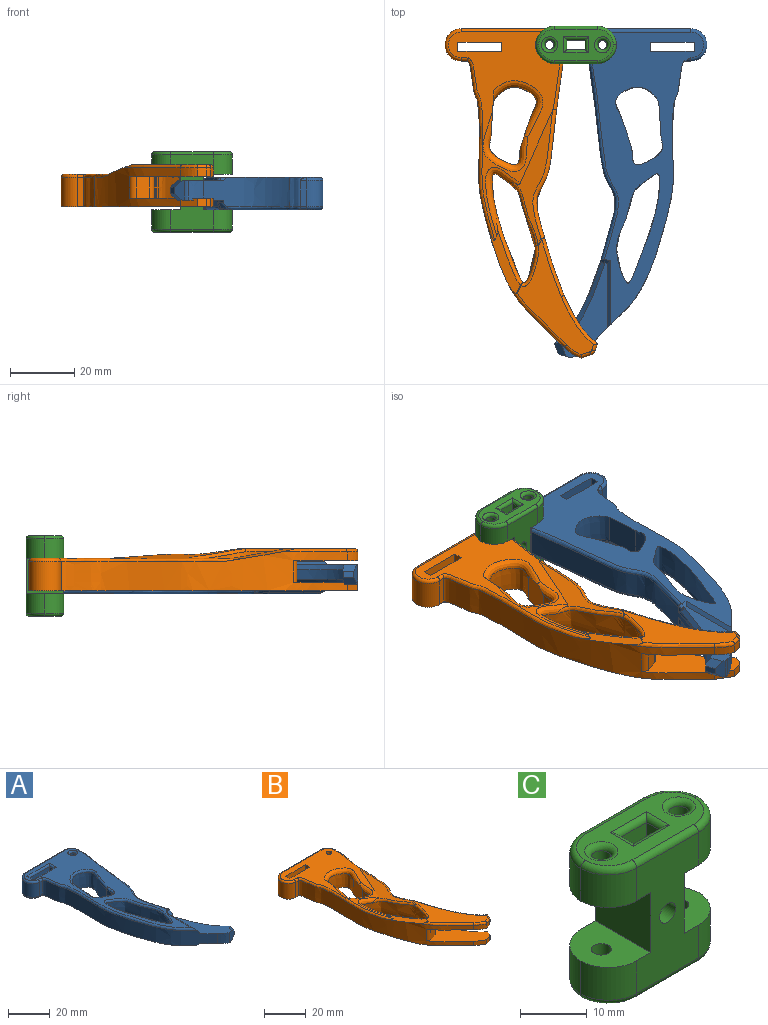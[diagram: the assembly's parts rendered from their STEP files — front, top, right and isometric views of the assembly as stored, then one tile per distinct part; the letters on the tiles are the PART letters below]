
ASSEMBLY  parts=3 mates=1
PART A: 74 faces, bbox 48.7x103.1x14 mm
  f0: plane 6x3.17mm, normal (0.32,-0.95,0), area 14.9mm2, adj f1,f25,f27,f28,f29,f30
  f1: plane 3.17x2mm, normal (0.94,-0.35,0), area 6.8mm2, adj f0,f2,f29,f30
  f2: extruded ~18.6x12mm, area 56.7mm2, adj f1,f8,f29,f30,f31,f33,f36,f45
  f3: extruded ~6x4.74mm, area 34.4mm2, adj f4,f25,f27,f28
  f4: extruded ~89.8x31.96mm, area 853mm2, adj f3,f7,f9,f14,f27,f28,f35,f44
  f5: plane 0.21x0.2mm, normal (0,-1,0), area 0mm2, adj f32,f37,f58
  f6: plane 88.13x34.8mm, normal (0,0,1), area 889.6mm2, adj f48,f49,f50,f51,f52,f53,f54,f60
  f7: plane 16.61x1mm, normal (1,0,0), area 16.6mm2, adj f4,f28,f35,f55
  f8: extruded ~72.26x8.46mm, area 526.1mm2, adj f2,f17,f36,f37,f38,f45,f46,f47
  f9: plane 91.35x34.8mm, normal (0,0,-1), area 1198.8mm2, adj f4,f10,f11,f15,f16,f20,f21,f22
  f10: plane 9x2.8mm, normal (1,0,0), area 25.2mm2, adj f9,f11,f15,f64
  f11: plane 13.5x9mm, normal (0,-1,0), area 121.5mm2, adj f9,f10,f26,f65
  f12: plane 8x4.46mm, normal (1,0,0), area 35.7mm2, adj f17,f19,f40,f50
  f13: plane 26.8x8mm, normal (0,1,0), area 214.4mm2, adj f18,f19,f42,f52
  f14: plane 8x1.91mm, normal (0,-1,0), area 15.3mm2, adj f4,f18,f44,f54
  f15: plane 13.5x9mm, normal (0,1,0), area 121.5mm2, adj f9,f10,f26,f66
  f16: cylinder r=1.35mm len=9mm, axis (0,0,-1), area 76.3mm2, adj f9,f73
  f17: cylinder r=5mm len=8mm, axis (0,0,-1), area 8.3mm2, adj f8,f12,f39,f49
  f18: cylinder r=5mm len=10mm, axis (0,0,-1), area 125.7mm2, adj f13,f14,f43,f53
  f19: cylinder r=5mm len=8mm, axis (0,0,-1), area 62.8mm2, adj f12,f13,f41,f51
  f20: plane 10.74x9mm, normal (1,-0.07,0), area 96.9mm2, adj f9,f22,f23,f72
  f21: plane 9.52x9mm, normal (-0.95,0.32,0), area 90.3mm2, adj f9,f22,f23,f69
  f22: extruded ~9.54x9mm, area 171.6mm2, adj f9,f20,f21,f71
  f23: extruded ~13.45x9.47mm, area 206.2mm2, adj f9,f20,f21,f70
  f24: extruded ~33.87x13.43mm, area 682.4mm2, adj f9,f68
  f25: cylinder r=2mm len=6mm, axis (0,0,-1), area 7.9mm2, adj f0,f3,f27,f28
  f26: plane 9x2.8mm, normal (-1,0,0), area 25.2mm2, adj f9,f11,f15,f67
  f27: plane 29.9x14.84mm, normal (0,0,-1), area 164.3mm2, adj f0,f3,f4,f25,f29,f31,f32,f57
  f28: plane 29.45x14.83mm, normal (0,0,1), area 163.1mm2, adj f0,f3,f4,f7,f25,f30,f33,f34
  f29: plane 4.39x3.74mm, normal (0.66,-0.25,-0.71), area 11.1mm2, adj f0,f1,f2,f27,f31
  f30: plane 4.39x3.74mm, normal (0.66,-0.25,0.71), area 11.1mm2, adj f0,f1,f2,f28,f33
  f31: bspline ~20.16x13.77mm, area 38.5mm2, adj f2,f27,f29,f32,f36
  f32: bspline ~11.58x5.44mm, area 19.2mm2, adj f5,f27,f31,f36,f37
  f33: bspline ~20.16x13.77mm, area 38.5mm2, adj f2,f28,f30,f34,f45
  f34: bspline ~11.59x5.44mm, area 18.8mm2, adj f28,f33,f45,f46,f55
  f35: plane 18.48x1.82mm, normal (0.71,0,0.71), area 41mm2, adj f4,f7,f55,f56,f60,f61
  f36: bspline ~13.74x5.23mm, area 7.6mm2, adj f2,f8,f31,f32,f37
  f37: cylinder r=1mm len=1.91mm, axis (0,0,-1), area 2mm2, adj f5,f8,f32,f36,f59
  f38: bspline ~63.26x9.43mm, area 98.7mm2, adj f8,f9,f39,f59
  f39: torus R=4mm, axis (0,0,1), area 1.5mm2, adj f9,f17,f38,f40
  f40: cylinder r=1mm len=4.46mm, axis (0,1,0), area 7mm2, adj f9,f12,f39,f41
  f41: torus R=4mm, axis (0,0,1), area 11.4mm2, adj f9,f19,f40,f42
  f42: cylinder r=1mm len=26.8mm, axis (-1,0,0), area 42.1mm2, adj f9,f13,f41,f43
  f43: torus R=4mm, axis (0,0,1), area 22.9mm2, adj f9,f18,f42,f44
  f44: cylinder r=1mm len=1.91mm, axis (1,0,0), area 1.9mm2, adj f4,f9,f14,f43
  f45: bspline ~13.74x5.23mm, area 7.6mm2, adj f2,f8,f33,f34,f46
  f46: cylinder r=1mm len=2.89mm, axis (0,0,-1), area 2.5mm2, adj f8,f34,f45,f47,f55
  f47: bspline ~9.08x8.98mm, area 3.3mm2, adj f8,f46,f55,f56,f63
  f48: bspline ~63.91x9.43mm, area 96.4mm2, adj f6,f8,f49,f63
  f49: torus R=4mm, axis (0,0,1), area 1.5mm2, adj f6,f17,f48,f50
  f50: cylinder r=1mm len=4.46mm, axis (0,-1,0), area 7mm2, adj f6,f12,f49,f51
  f51: torus R=4mm, axis (0,0,1), area 11.4mm2, adj f6,f19,f50,f52
  f52: cylinder r=1mm len=26.8mm, axis (1,0,0), area 42.1mm2, adj f6,f13,f51,f53
  f53: torus R=4mm, axis (0,0,1), area 22.9mm2, adj f6,f18,f52,f54
  f54: cylinder r=1mm len=2.16mm, axis (-1,0,0), area 3.2mm2, adj f6,f14,f53,f60
  f55: cylinder r=5mm len=3.7mm, axis (0,0,-1), area 4.3mm2, adj f7,f28,f34,f35,f46,f47,f56
  f56: bspline ~5.24x4mm, area 9.4mm2, adj f35,f47,f55,f62
  f57: plane 21.04x1.04mm, normal (0.71,0,-0.71), area 28.4mm2, adj f4,f9,f27,f58
  f58: plane 1.96x1mm, normal (0,-0.71,-0.71), area 2.1mm2, adj f5,f9,f27,f57,f59
  f59: bspline ~1.29x1.02mm, area 0.9mm2, adj f37,f38,f58
  f60: bspline ~83.73x24.93mm, area 136.1mm2, adj f4,f6,f35,f54,f61
  f61: cylinder r=1mm len=16.39mm, axis (0,1,0), area 12.2mm2, adj f6,f35,f60,f62
  f62: bspline ~4.48x4.05mm, area 3.5mm2, adj f6,f56,f61,f63
  f63: sphere r=1mm, area 0.8mm2, adj f47,f48,f62
  f64: cylinder r=1mm len=4.8mm, axis (0,-1,0), area 6mm2, adj f6,f10,f65,f66
  f65: cylinder r=1mm len=15.5mm, axis (-1,0,0), area 22.8mm2, adj f6,f11,f64,f67
  f66: cylinder r=1mm len=15.5mm, axis (1,0,0), area 22.8mm2, adj f6,f15,f64,f67
  f67: cylinder r=1mm len=4.8mm, axis (0,1,0), area 6mm2, adj f6,f26,f65,f66
  f68: bspline ~35.94x15.5mm, area 122.3mm2, adj f6,f24
  f69: cylinder r=1mm len=9.84mm, axis (-0.32,-0.95,0), area 15.6mm2, adj f6,f21,f70,f71
  f70: bspline ~15.49x11.88mm, area 37.9mm2, adj f6,f23,f69,f72
  f71: bspline ~11.62x11.16mm, area 31.7mm2, adj f6,f22,f69,f72
  f72: cylinder r=1mm len=10.89mm, axis (0.07,1,0), area 16.9mm2, adj f6,f20,f70,f71
  f73: torus R=2.35mm, axis (0,0,1), area 16.9mm2, adj f6,f16
PART B: 70 faces, bbox 61.7x121x14.4 mm
  f0: plane 2.5x2.27mm, normal (0.94,-0.35,0), area 6.1mm2, adj f3,f17,f38,f52
  f1: plane 2.85x2.5mm, normal (0.32,-0.95,0), area 7.5mm2, adj f17,f27,f38,f52
  f2: extruded ~88.8x30.06mm, area 833.9mm2, adj f11,f17,f18,f27,f30,f32,f52,f56
  f3: extruded ~2.5x0.02mm, area 0mm2, adj f0,f16,f17,f52
  f4: plane 64.7x34.89mm, normal (0,0,1), area 630mm2, adj f9,f10,f12,f13,f14,f31,f32,f40
  f5: extruded ~72.26x12mm, area 630.7mm2, adj f6,f16,f17,f21,f30,f36,f47,f48
  f6: extruded ~14.96x10.43mm, area 49.8mm2, adj f5,f20,f30,f64
  f7: plane 9x4.46mm, normal (1,0,0), area 40.2mm2, adj f17,f21,f23,f45
  f8: plane 26.8x9mm, normal (0,1,0), area 241.2mm2, adj f17,f22,f23,f43
  f9: plane 10x2.8mm, normal (1,0,0), area 28mm2, adj f4,f10,f12,f17
  f10: plane 13.5x10mm, normal (0,-1,0), area 135mm2, adj f4,f9,f17,f40
  f11: plane 9x1.91mm, normal (0,-1,0), area 17.2mm2, adj f2,f17,f22,f41
  f12: plane 13.5x10mm, normal (0,1,0), area 135mm2, adj f4,f9,f17,f40
  f13: cylinder r=1.35mm len=10mm, axis (0,0,-1), area 84.8mm2, adj f4,f17
  f14: plane 15.17x10.31mm, normal (1,-0.07,0), area 106.4mm2, adj f4,f17,f24,f25,f50,f51
  f15: plane 10.55x10.45mm, normal (-0.95,0.32,0), area 91.7mm2, adj f17,f24,f25,f50,f51
  f16: extruded ~14.96x10.42mm, area 46.1mm2, adj f3,f5,f17,f52
  f17: plane 102.15x47.37mm, normal (0,0,-1), area 1552.6mm2, adj f0,f1,f2,f3,f5,f7,f8,f9
  f18: extruded ~5.45x3.36mm, area 17.5mm2, adj f2,f19,f30,f60
  f19: plane 2.85x2.7mm, normal (0.32,-0.95,0), area 8.1mm2, adj f18,f30,f39,f61
  f20: plane 2.7x2.28mm, normal (0.94,-0.35,0), area 6.6mm2, adj f6,f30,f39,f63
  f21: cylinder r=5mm len=9mm, axis (0,0,-1), area 9.4mm2, adj f5,f7,f17,f46
  f22: cylinder r=5mm len=10mm, axis (0,0,-1), area 141.4mm2, adj f8,f11,f17,f42
  f23: cylinder r=5mm len=9mm, axis (0,0,-1), area 70.7mm2, adj f7,f8,f17,f44
  f24: extruded ~9.54x8.47mm, area 152.5mm2, adj f14,f15,f17,f51
  f25: extruded ~13.45x9.47mm, area 183.3mm2, adj f14,f15,f17,f50
  f26: extruded ~33.87x13.43mm, area 752mm2, adj f17,f49,f53,f54,f55
  f27: plane 5.45x3.36mm, normal (-0.52,-0.85,0), area 16mm2, adj f1,f2,f17,f52
  f28: plane 14.35x6.8mm, normal (1,0,0), area 97.6mm2, adj f30,f35,f37,f52
  f29: plane 35.89x23.75mm, normal (0,0,1), area 267mm2, adj f54,f58,f59,f60,f61,f62,f63,f64
  f30: plane 40.23x26.26mm, normal (0,0,-1), area 314.1mm2, adj f2,f5,f6,f18,f19,f20,f28,f33
  f31: plane 42.46x12.15mm, normal (-0.21,0.09,0.97), area 132.3mm2, adj f4,f48,f49,f53,f67
  f32: plane 22.72x11.46mm, normal (-0.21,0.09,0.97), area 55mm2, adj f2,f4,f49,f55,f56,f58,f59
  f33: plane 6.8x4mm, normal (0.31,-0.95,0), area 28.5mm2, adj f30,f37,f52,f69
  f34: plane 6.8x0.54mm, normal (0.8,-0.6,0), area 4.6mm2, adj f30,f35,f36,f52
  f35: cylinder r=2mm len=6.8mm, axis (0,0,1), area 8.7mm2, adj f28,f30,f34,f52
  f36: cylinder r=2mm len=6.8mm, axis (0,0,-1), area 12.6mm2, adj f5,f30,f34,f52
  f37: cylinder r=2mm len=6.8mm, axis (0,0,-1), area 17.1mm2, adj f28,f30,f33,f52
  f38: cylinder r=2mm len=2.5mm, axis (0,0,-1), area 4.4mm2, adj f0,f1,f17,f52
  f39: cylinder r=2mm len=2.7mm, axis (0,0,-1), area 4.8mm2, adj f19,f20,f30,f62
  f40: plane 10x2.8mm, normal (-1,0,0), area 28mm2, adj f4,f10,f12,f17
  f41: cylinder r=1mm len=2.16mm, axis (-1,0,0), area 3.2mm2, adj f4,f11,f42,f56
  f42: torus R=4mm, axis (0,0,1), area 22.9mm2, adj f4,f22,f41,f43
  f43: cylinder r=1mm len=26.8mm, axis (1,0,0), area 42.1mm2, adj f4,f8,f42,f44
  f44: torus R=4mm, axis (0,0,1), area 11.4mm2, adj f4,f23,f43,f45
  f45: cylinder r=1mm len=4.46mm, axis (0,-1,0), area 7mm2, adj f4,f7,f44,f46
  f46: torus R=4mm, axis (0,0,1), area 1.5mm2, adj f4,f21,f45,f47
  f47: bspline ~20.78x3.84mm, area 23.4mm2, adj f4,f5,f46,f48
  f48: bspline ~43.13x7.53mm, area 73.3mm2, adj f4,f5,f31,f47,f66
  f49: bspline ~22.17x11.29mm, area 74.7mm2, adj f4,f26,f31,f32,f53,f55
  f50: bspline ~20.89x17.45mm, area 86.8mm2, adj f4,f14,f15,f25,f51
  f51: bspline ~19.31x14.37mm, area 85.6mm2, adj f4,f14,f15,f24,f50
  f52: plane 40.23x26.26mm, normal (0,0,1), area 312.4mm2, adj f0,f1,f2,f3,f5,f16,f27,f28
  f53: bspline ~22.07x10.64mm, area 31.2mm2, adj f26,f31,f49,f68
  f54: bspline ~14.29x5.61mm, area 21.3mm2, adj f26,f29,f57,f68
  f55: bspline ~26.94x10.34mm, area 37.6mm2, adj f26,f32,f49,f57
  f56: bspline ~58.44x9.36mm, area 85.8mm2, adj f2,f4,f32,f41
  f57: sphere r=1mm, area 0.2mm2, adj f54,f55,f58
  f58: cylinder r=1mm len=2.78mm, axis (-0.41,-0.91,0), area 0.7mm2, adj f29,f32,f57,f59
  f59: bspline ~43.59x42.05mm, area 37.4mm2, adj f2,f29,f32,f58,f60
  f60: bspline ~6.96x5.05mm, area 9.6mm2, adj f18,f29,f59,f61
  f61: cylinder r=1mm len=3.18mm, axis (-0.95,-0.32,0), area 4.5mm2, adj f19,f29,f60,f62
  f62: torus R=1mm, axis (0,0,1), area 2.3mm2, adj f29,f39,f61,f63
  f63: cylinder r=1mm len=2.64mm, axis (-0.35,-0.94,0), area 3.2mm2, adj f20,f29,f62,f64
  f64: bspline ~19.2x12.99mm, area 28.7mm2, adj f6,f29,f63,f65
  f65: bspline ~23.02x8.88mm, area 29.6mm2, adj f5,f29,f64,f66
  f66: sphere r=1mm, area 0.3mm2, adj f48,f65,f67
  f67: cylinder r=1mm len=2.2mm, axis (-0.41,-0.91,0), area 0.5mm2, adj f29,f31,f66,f68
  f68: sphere r=1mm, area 0.1mm2, adj f53,f54,f67
  f69: cylinder r=2mm len=6.8mm, axis (0,0,-1), area 17.9mm2, adj f2,f30,f33,f52
PART C: 52 faces, bbox 26.1x12.7x25 mm
  f0: plane 23x13.1mm, normal (0,1,0), area 226.2mm2, adj f12,f13,f14,f15,f17,f19,f21,f23
  f1: plane 23x13.1mm, normal (0,-1,0), area 226.2mm2, adj f12,f13,f14,f15,f16,f18,f20,f22
  f2: cylinder r=1.5mm len=6mm, axis (0,0,1), area 56.5mm2, adj f14,f46
  f3: cylinder r=1.5mm len=6mm, axis (0,0,1), area 56.5mm2, adj f12,f48
  f4: plane 23.1x9.7mm, normal (0,0,1), area 124.8mm2, adj f26,f27,f28,f29,f30,f31,f38,f39
  f5: plane 23.1x9.7mm, normal (0,0,-1), area 124.8mm2, adj f32,f33,f34,f35,f36,f37,f42,f43
  f6: plane 23x5.7mm, normal (0,-1,0), area 122mm2, adj f7,f9,f17,f41,f45
  f7: plane 23x3mm, normal (1,0,0), area 69mm2, adj f6,f8,f39,f43
  f8: plane 23x5.7mm, normal (0,1,0), area 122mm2, adj f7,f9,f16,f38,f42
  f9: plane 23x3mm, normal (-1,0,0), area 69mm2, adj f6,f8,f40,f44
  f10: cylinder r=1.5mm len=6mm, axis (0,0,1), area 56.5mm2, adj f15,f47
  f11: cylinder r=1.5mm len=6mm, axis (0,0,1), area 56.5mm2, adj f13,f49
  f12: plane 11.7x9mm, normal (0,0,-1), area 82.8mm2, adj f0,f1,f3,f22,f23,f50
  f13: plane 11.7x9mm, normal (0,0,1), area 82.8mm2, adj f0,f1,f11,f20,f21,f50
  f14: plane 11.7x9mm, normal (0,0,-1), area 82.8mm2, adj f0,f1,f2,f24,f25,f51
  f15: plane 11.7x9mm, normal (0,0,1), area 82.8mm2, adj f0,f1,f10,f18,f19,f51
  f16: cylinder r=1.7mm len=4.35mm, axis (0,-1,0), area 46.5mm2, adj f1,f8
  f17: cylinder r=1.7mm len=4.35mm, axis (0,-1,0), area 46.5mm2, adj f0,f6
  f18: cylinder r=6mm len=6mm, axis (0,0,1), area 55.6mm2, adj f1,f15,f19,f32
  f19: cylinder r=6mm len=6mm, axis (0,0,-1), area 55.6mm2, adj f0,f15,f18,f34
  f20: cylinder r=6mm len=6mm, axis (0,0,-1), area 55.6mm2, adj f1,f13,f21,f35
  f21: cylinder r=6mm len=6mm, axis (0,0,1), area 55.6mm2, adj f0,f13,f20,f37
  f22: cylinder r=6mm len=6mm, axis (0,0,-1), area 55.6mm2, adj f1,f12,f23,f30
  f23: cylinder r=6mm len=6mm, axis (0,0,1), area 55.6mm2, adj f0,f12,f22,f31
  f24: cylinder r=6mm len=6mm, axis (0,0,-1), area 55.6mm2, adj f0,f14,f25,f27
  f25: cylinder r=6mm len=6mm, axis (0,0,1), area 55.6mm2, adj f1,f14,f24,f26
  f26: torus R=5mm, axis (0,0,1), area 13.7mm2, adj f4,f25,f27,f28
  f27: torus R=5mm, axis (0,0,1), area 13.7mm2, adj f4,f24,f26,f29
  f28: cylinder r=1mm len=13.1mm, axis (-1,0,0), area 20.6mm2, adj f1,f4,f26,f30
  f29: cylinder r=1mm len=13.1mm, axis (1,0,0), area 20.6mm2, adj f0,f4,f27,f31
  f30: torus R=5mm, axis (0,0,1), area 13.7mm2, adj f4,f22,f28,f31
  f31: torus R=5mm, axis (0,0,1), area 13.7mm2, adj f4,f23,f29,f30
  f32: torus R=5mm, axis (0,0,1), area 13.7mm2, adj f5,f18,f33,f34
  f33: cylinder r=1mm len=13.1mm, axis (1,0,0), area 20.6mm2, adj f1,f5,f32,f35
  f34: torus R=5mm, axis (0,0,1), area 13.7mm2, adj f5,f19,f32,f36
  f35: torus R=5mm, axis (0,0,1), area 13.7mm2, adj f5,f20,f33,f37
  f36: cylinder r=1mm len=13.1mm, axis (-1,0,0), area 20.6mm2, adj f0,f5,f34,f37
  f37: torus R=5mm, axis (0,0,1), area 13.7mm2, adj f5,f21,f35,f36
  f38: cylinder r=1mm len=7.7mm, axis (-1,0,0), area 10.1mm2, adj f4,f8,f39,f40
  f39: cylinder r=1mm len=5mm, axis (0,1,0), area 5.9mm2, adj f4,f7,f38,f41
  f40: cylinder r=1mm len=5mm, axis (0,-1,0), area 5.9mm2, adj f4,f9,f38,f41
  f41: cylinder r=1mm len=7.7mm, axis (1,0,0), area 10.1mm2, adj f4,f6,f39,f40
  f42: cylinder r=1mm len=7.7mm, axis (1,0,0), area 10.1mm2, adj f5,f8,f43,f44
  f43: cylinder r=1mm len=5mm, axis (0,-1,0), area 5.9mm2, adj f5,f7,f42,f45
  f44: cylinder r=1mm len=5mm, axis (0,1,0), area 5.9mm2, adj f5,f9,f42,f45
  f45: cylinder r=1mm len=7.7mm, axis (-1,0,0), area 10.1mm2, adj f5,f6,f43,f44
  f46: torus R=2.5mm, axis (0,0,1), area 18.4mm2, adj f2,f4
  f47: torus R=2.5mm, axis (0,0,1), area 18.4mm2, adj f5,f10
  f48: torus R=2.5mm, axis (0,0,1), area 18.4mm2, adj f3,f4
  f49: torus R=2.5mm, axis (0,0,1), area 18.4mm2, adj f5,f11
  f50: plane 11.7x11mm, normal (-1,0,0), area 128.7mm2, adj f0,f1,f12,f13
  f51: plane 11.7x11mm, normal (1,0,0), area 128.7mm2, adj f0,f1,f14,f15
PLACE A rot(axis=(0,1,0),180deg) t=(20,21.96,16)mm
PLACE B t=(-63.41,21.96,7)mm
PLACE C t=(0,0,-1)mm
MATE revolute B.f13 <-> C.f3  axis (0,0,-1) through (-57.45,26.38,17)mm
